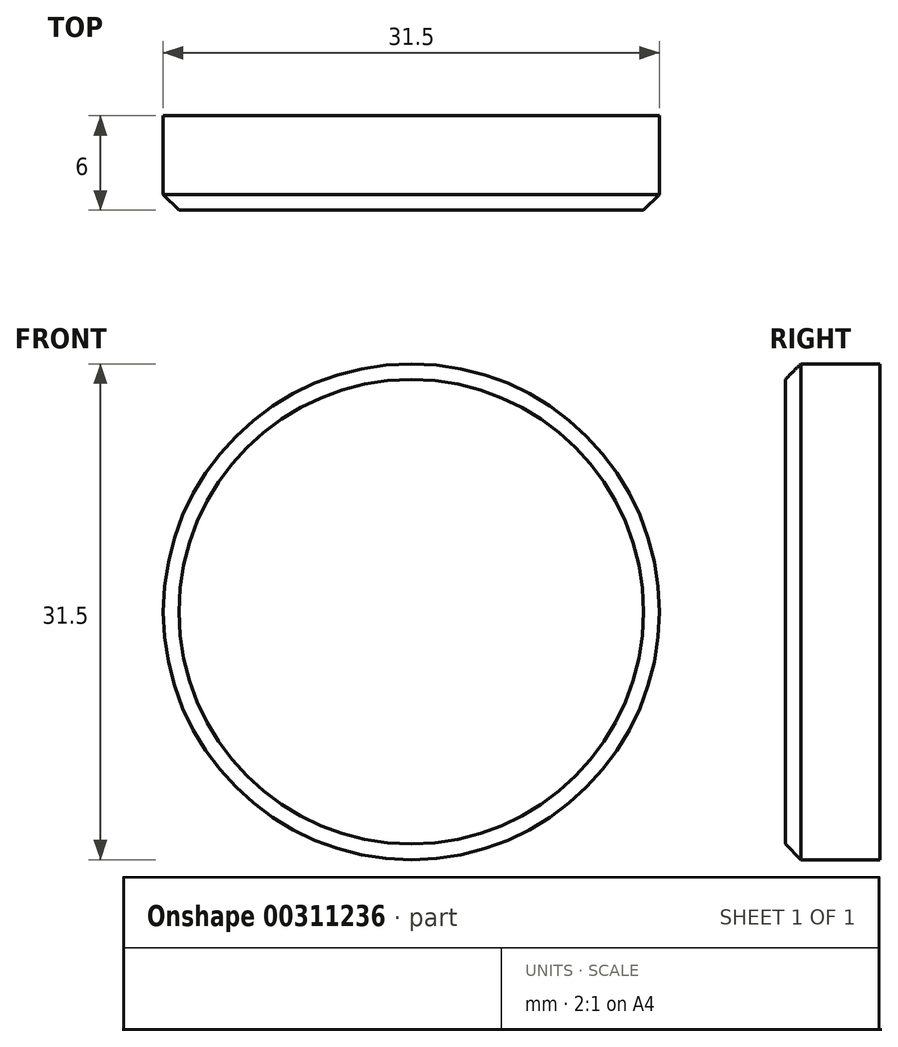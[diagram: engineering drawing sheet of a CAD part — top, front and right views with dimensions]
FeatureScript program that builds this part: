
annotation { "Feature Type Name" : "Feature", "Feature Type Description" : "" }
export const myFeature = defineFeature(function(context is Context, id is Id, definition is map)
    precondition{}
    {
        {
            var Q0;
            Q0=qCreatedBy(makeId("Right.planeOp"),FACE);
            var sketch = newSketch(context, id + "F0", { "sketchPlane" : qUnion([Q0])});
            skLineSegment(sketch, "E0.bottom", {"start": v(0, 0) * mm, "end": v(-12, 0) * mm});
            skLineSegment(sketch, "E0.top", {"start": v(0, 39) * mm, "end": v(-12, 39) * mm});
            skLineSegment(sketch, "E0.left", {"start": v(0, 0) * mm, "end": v(0, 39) * mm});
            skLineSegment(sketch, "E0.right", {"start": v(-12, 0) * mm, "end": v(-12, 39) * mm});
            skLineSegment(sketch, "E1.bottom", {"start": v(-12, 39) * mm, "end": v(-5.7, 39) * mm});
            skLineSegment(sketch, "E1.top", {"start": v(-12, 31.5) * mm, "end": v(-5.7, 31.5) * mm});
            skLineSegment(sketch, "E1.left", {"start": v(-12, 39) * mm, "end": v(-12, 31.5) * mm});
            skLineSegment(sketch, "E1.right", {"start": v(-5.7, 39) * mm, "end": v(-5.7, 31.5) * mm});
            skLineSegment(sketch, "E2", {"start": v(18.3, 0) * mm, "end": v(-48.83, 0) * mm, "construction": true});
            skLineSegment(sketch, "E3.bottom", {"start": v(-12, 15.75) * mm, "end": v(-6, 15.75) * mm});
            skLineSegment(sketch, "E3.top", {"start": v(-12, 0) * mm, "end": v(-6, 0) * mm});
            skLineSegment(sketch, "E3.left", {"start": v(-12, 15.75) * mm, "end": v(-12, 0) * mm});
            skLineSegment(sketch, "E3.right", {"start": v(-6, 15.75) * mm, "end": v(-6, 0) * mm});
            skSolve(sketch);
        }
        {
            var Q0;
            Q0=makeQuery(id+"F0.imprint","IMPRINT",FACE,{"disambiguationData":[TD([[makeQuery(id+"F0.imprint","IMPRINT",EDGE,{"derivedFrom":sQuery(id+"F0.wireOp",EDGE,"E0.bottom")}),-1.0]])]});
            var Q1;
            Q1=sQuery(id+"F0.wireOp",EDGE,"E2");
            revolve(context, id + "F1", {"entities" : qUnion([Q0]), "axis" : qUnion([Q1]), "revolveType" : RevolveType.FULL});
        }
        {
            var Q0;
            Q0=qCreatedBy(makeId("Front.planeOp"),FACE);
            var sketch = newSketch(context, id + "F2", { "sketchPlane" : qUnion([Q0])});
            skCircle(sketch, "E4", {"center": v(0, 0) * mm, "radius": 25 * mm, "construction": true});
            skPoint(sketch, "E5", {"position": v(0, 25) * mm});
            skLineSegment(sketch, "E6", {"start": v(0, 0) * mm, "end": v(32.66, 32.66) * mm, "construction": true});
            skLineSegment(sketch, "E7", {"start": v(0, 0) * mm, "end": v(0, 44.56) * mm, "construction": true});
            skPoint(sketch, "E8", {"position": v(17.68, 17.68) * mm});
            skSolve(sketch);
        }
        {
            var Q0;
            Q0=sQuery(id+"F2.wireOp",VERTEX,"E5");
            var Q1;
            Q1=makeQuery(id+"F1.opRevolve","SWEPT_BODY",BODY,{"disambiguationData":[OSD([sQuery(id+"F0.wireOp",EDGE,"E0.bottom"),sQuery(id+"F0.wireOp",EDGE,"E0.top"),sQuery(id+"F0.wireOp",EDGE,"E0.left"),sQuery(id+"F0.wireOp",EDGE,"E0.right"),sQuery(id+"F0.wireOp",EDGE,"E1.top"),sQuery(id+"F0.wireOp",EDGE,"E1.right")])]});
            hole(context, id + "F3", {"style" : HoleStyle.SIMPLE, "endStyle" : HoleEndStyle.THROUGH, "oppositeDirection" : true, "holeDiameter" : 6 * mm, "tappedDepth" : 12 * mm, "tapClearance" : 3, "locations" : qUnion([Q0]), "scope" : qUnion([Q1])});
        }
        {
            var Q0;
            Q0=makeQuery(id+"F1.opRevolve","SWEPT_EDGE",EDGE,{"disambiguationData":[OSD([sQuery(id+"F0.wireOp",EDGE,"E0.right"),sQuery(id+"F0.wireOp",EDGE,"E3.bottom"),sQuery(id+"F0.wireOp",EDGE,"E3.left")])]});
            var Q1;
            Q1=makeQuery(id+"F1.opRevolve","SWEPT_EDGE",EDGE,{"disambiguationData":[OSD([sQuery(id+"F0.wireOp",EDGE,"E0.right"),sQuery(id+"F0.wireOp",EDGE,"E1.top"),sQuery(id+"F0.wireOp",EDGE,"E1.left")])]});
            var Q2;
            Q2=makeQuery(id+"F1.opRevolve","SWEPT_EDGE",EDGE,{"disambiguationData":[OSD([sQuery(id+"F0.wireOp",EDGE,"E0.top"),sQuery(id+"F0.wireOp",EDGE,"E1.bottom"),sQuery(id+"F0.wireOp",EDGE,"E1.right")])]});
            chamfer(context, id + "F4", {"entities" : qUnion([Q0, Q1, Q2]), "width" : 1 * mm, "tangentPropagation" : true});
        }
    });
